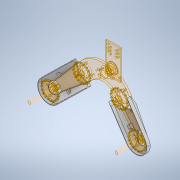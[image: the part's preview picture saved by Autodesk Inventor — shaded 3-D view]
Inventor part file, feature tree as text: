
AUTODESK INVENTOR PART (.ipt)
format: ipt  version: 2020.1 (Build 241239000, 239)  size: 4,801,536 bytes
history: native  units: mm
features: other x27, surface_op x12, sketch x10, extrude x6, plane x2, loft x2, shell x2, hole x2, chamfer x2, projected_geometry x2
ambient origin geometry x8: Origin, YZ Plane, XZ Plane, XY Plane, X Axis, Y Axis, Z Axis, Center Point
bodies: body (feature_tree)
feature tree (67):
  other  "Lenkerhuelle V2"
  plane  "Work Plane1"
  sketch  "Sketch1"  dims[d0=3.0mm d1=3.0mm]
  sketch  "Sketch2"  dims[d2=3.0mm d3=3.0mm]
  plane  "Work Plane2"
  sketch  "Sketch3"  dims[d4=3.0mm d5=5.0mm d6=75.0mm]
  sketch  "Sketch4"  dims[d8=75.0mm d9=75.0mm d10=0.0mm d11=90.0deg]
  loft  "Loft1"
  loft  "Loft2"
  extrude  "Extrusion3"  Depth=5.0mm
  shell  "Shell3"  Thickness=75.0mm
  extrude  "Extrusion4"  Depth=75.0mm
  shell  "Shell4"  Thickness=0.0mm
  sketch  "Sketch10"  dims[d27=11.0mm d28=0.0mm d29=35.0mm]
  hole  "Hole1"  [1 undecoded]
  hole  "Hole2"  [1 undecoded]
  sketch  "Sketch11"  dims[d30=35.0mm d31=2.0mm]
  extrude  "Extrusion5"  Depth=35.0mm
  extrude  "Extrusion6"  Depth=2.0mm
  extrude  "Extrusion7"  Depth=1.0mm
  chamfer  "Chamfer1"  Distance=1.0mm
  extrude  "Extrusion8"  Depth=2.0mm TaperAngle=0.0deg
  chamfer  "Chamfer2"  Distance=23.7mm
  other  "Lenkerhuelle V1"
  sketch  "Sketch8"  dims[d12=0.0mm d13=90.0deg d14=0.0mm d15=90.0deg d16=0.0mm d17=90.0deg]
  projected_geometry  "Projected Loop3"
  sketch  "Sketch9"  dims[d24=11.0mm d25=0.0mm d26=2.0mm]
  projected_geometry  "Projected Loop4"
  sketch  "Sketch12"  dims[d32=5.0mm d33=6.0mm d34=4.0mm d35=2.0mm d36=90.0deg d37=8.0mm d38=20.594885mm]
  sketch  "Sketch13"  dims[d39=5.0mm d40=6.0mm d41=4.0mm d42=2.0mm d43=90.0deg d44=8.0mm d45=20.594885mm d46=1.0mm d47=1.0mm d48=23.7mm d49=0.0mm d50=23.7mm d51=0.0mm d52=0.2mm d54=12.0mm d55=10.0mm d56=0.0mm d57=2.0mm d58=2.0mm d59=45.0deg d60=0.2mm d61=12.0mm d62=10.0mm d63=0.0mm d64=2.0mm d65=2.0mm d66=45.0deg]
  surface_op  "Surface1"
  surface_op  "Surface2"
  surface_op  "Surface3"
  surface_op  "Surface4"
  surface_op  "Surface5"
  surface_op  "Surface6"
  surface_op  "Surface7"
  surface_op  "Surface8"
  surface_op  "Surface9"
  surface_op  "Surface10"
  surface_op  "Surface11"
  surface_op  "Surface12"
  other  "Srf1"
  other  "Srf2"
  other  "Srf3"
  other  "Srf4"
  other  "Srf5"
  other  "Srf6"
  other  "Srf7"
  other  "Srf8"
  other  "Srf9"
  other  "Srf10"
  other  "Srf11"
  other  "Srf12"
  other  "<userpath>\Desktop\URBANT ROVER\rover.iam"
  other  "rover.iam"
  other  "swing R"
  other  "EXACT SWING.1"
  other  "Kettenradaufnahme.1"
  other  "swing axle connector.1"
  other  "Kettenradaufnahme.2"
  other  "Rad mit Aufnahme.5"
  other  "Axle Nut.2"
  other  "drive shaft.2"
  other  "Axle Nut.3"
  other  "drive shaft.1"
  other  "Rad mit Aufnahme.4"
note: 2 required parameter values undecoded (feature->parameter linkage not recoverable at this tier; creation-order binding heuristic only, values carry confidence <= 0.55)
